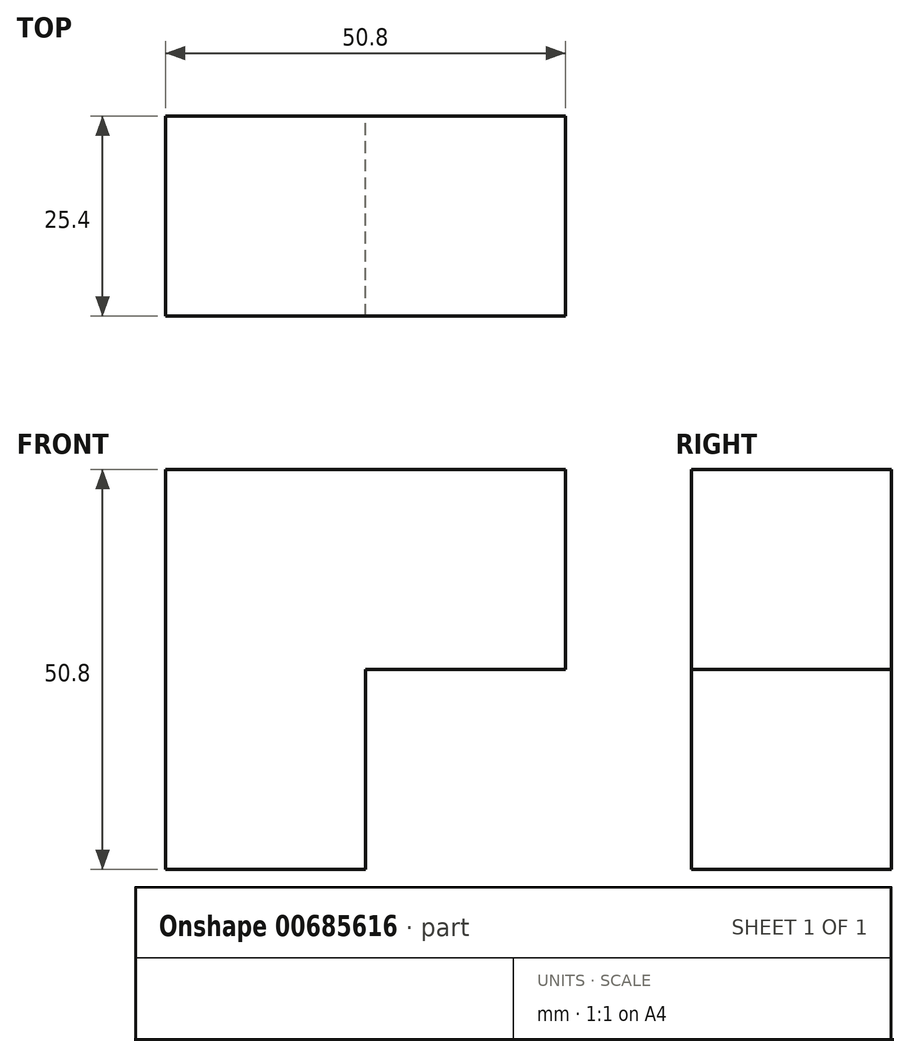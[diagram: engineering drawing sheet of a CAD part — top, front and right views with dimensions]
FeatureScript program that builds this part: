
annotation { "Feature Type Name" : "Feature", "Feature Type Description" : "" }
export const myFeature = defineFeature(function(context is Context, id is Id, definition is map)
    precondition{}
    {
        {
            var Q0;
            Q0=qCreatedBy(makeId("Front.planeOp"),FACE);
            var sketch = newSketch(context, id + "F0", { "sketchPlane" : qUnion([Q0])});
            skLineSegment(sketch, "E0", {"start": v(-56.05, 50.8) * mm, "end": v(-56.05, 0) * mm});
            skLineSegment(sketch, "E1", {"start": v(-56.05, 50.8) * mm, "end": v(-5.25, 50.8) * mm});
            skLineSegment(sketch, "E2", {"start": v(-5.25, 50.8) * mm, "end": v(-5.25, 25.4) * mm});
            skLineSegment(sketch, "E3", {"start": v(-5.25, 25.4) * mm, "end": v(-30.65, 25.4) * mm});
            skLineSegment(sketch, "E4", {"start": v(-30.65, 25.4) * mm, "end": v(-30.65, 0) * mm});
            skLineSegment(sketch, "E5", {"start": v(-30.65, 0) * mm, "end": v(-56.05, 0) * mm});
            skSolve(sketch);
        }
        {
            var Q0;
            Q0=makeQuery(id+"F0.imprint","IMPRINT",FACE,{"disambiguationData":[TD([[makeQuery(id+"F0.imprint","IMPRINT",EDGE,{"derivedFrom":sQuery(id+"F0.wireOp",EDGE,"E0")}),1.0]])]});
            extrude(context, id + "F1", {"entities" : qUnion([Q0]), "depth" : 25.4 * mm, "offsetDistance" : 25.4 * mm});
        }
    });
